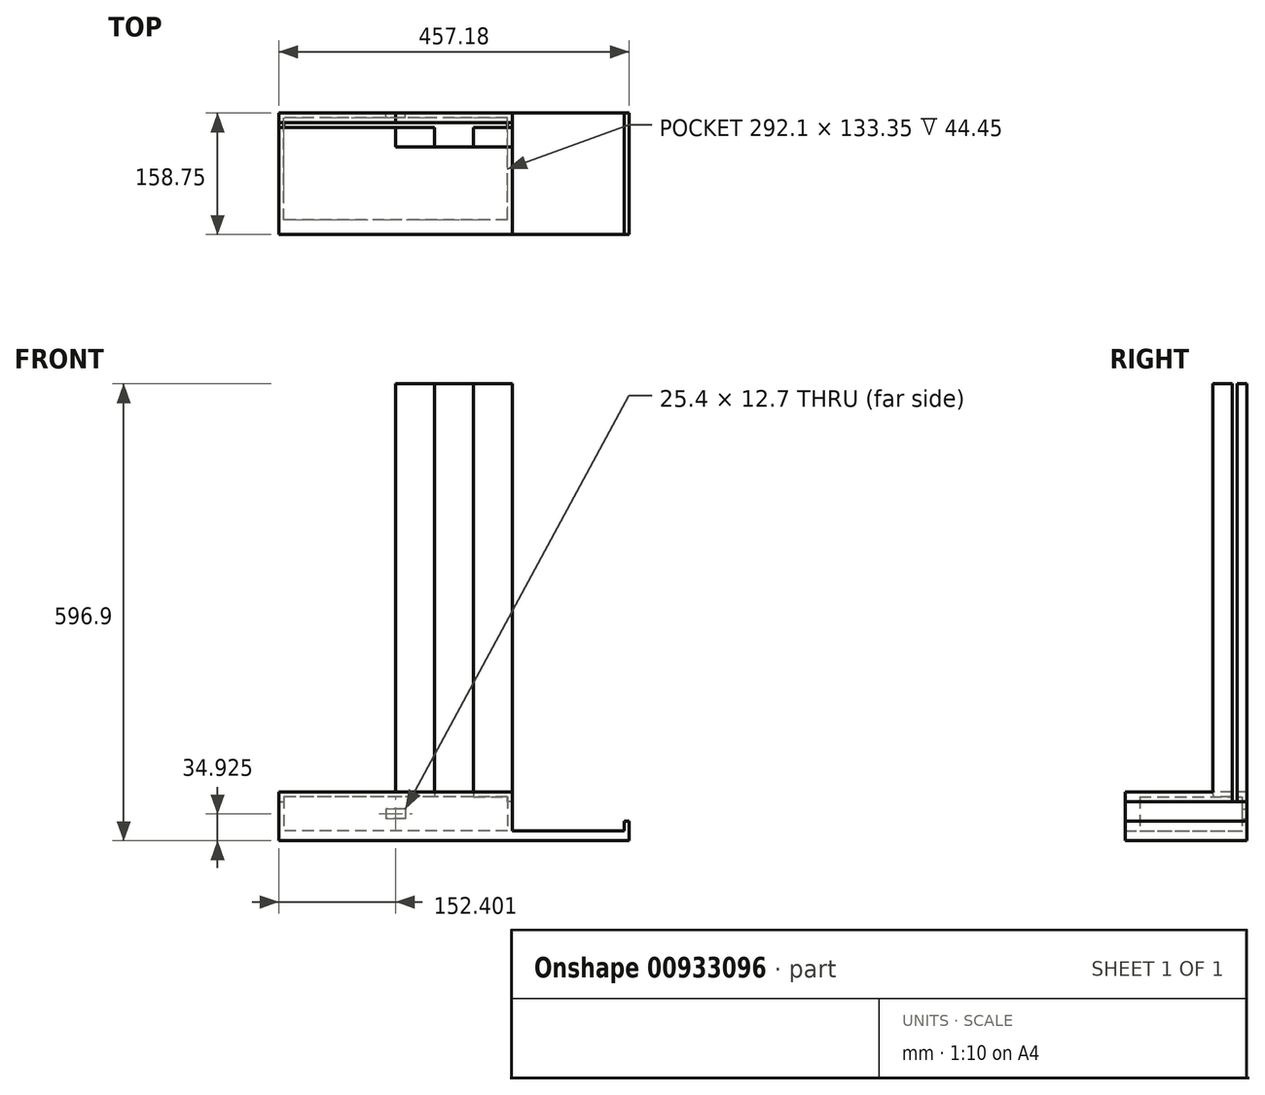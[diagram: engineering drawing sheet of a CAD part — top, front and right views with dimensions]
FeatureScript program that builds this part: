
annotation { "Feature Type Name" : "Feature", "Feature Type Description" : "" }
export const myFeature = defineFeature(function(context is Context, id is Id, definition is map)
    precondition{}
    {
        {
            var Q0;
            Q0=qCreatedBy(makeId("Top.planeOp"),FACE);
            var sketch = newSketch(context, id + "F0", { "sketchPlane" : qUnion([Q0])});
            skLineSegment(sketch, "E0.bottom", {"start": v(-59.49, 68.51) * mm, "end": v(-8.69, 68.51) * mm});
            skLineSegment(sketch, "E0.top", {"start": v(-59.49, 93.91) * mm, "end": v(-8.69, 93.91) * mm});
            skLineSegment(sketch, "E0.left", {"start": v(-59.49, 68.51) * mm, "end": v(-59.49, 93.91) * mm});
            skLineSegment(sketch, "E0.right", {"start": v(-8.69, 68.51) * mm, "end": v(-8.69, 93.91) * mm});
            skLineSegment(sketch, "E1.bottom", {"start": v(92.91, 68.51) * mm, "end": v(42.11, 68.51) * mm});
            skLineSegment(sketch, "E1.top", {"start": v(92.91, 93.91) * mm, "end": v(42.11, 93.91) * mm});
            skLineSegment(sketch, "E1.left", {"start": v(92.91, 68.51) * mm, "end": v(92.91, 93.91) * mm});
            skLineSegment(sketch, "E1.right", {"start": v(42.11, 68.51) * mm, "end": v(42.11, 93.91) * mm});
            skLineSegment(sketch, "E2.bottom", {"start": v(92.91, 93.91) * mm, "end": v(54.81, 93.91) * mm});
            skLineSegment(sketch, "E2.top", {"start": v(92.91, 100.26) * mm, "end": v(54.81, 100.26) * mm});
            skLineSegment(sketch, "E2.left", {"start": v(92.91, 93.91) * mm, "end": v(92.91, 100.26) * mm});
            skLineSegment(sketch, "E2.right", {"start": v(54.81, 93.91) * mm, "end": v(54.81, 100.26) * mm});
            skLineSegment(sketch, "E3.bottom", {"start": v(-59.49, 93.91) * mm, "end": v(-21.39, 93.91) * mm});
            skLineSegment(sketch, "E3.top", {"start": v(-59.49, 100.26) * mm, "end": v(-21.39, 100.26) * mm});
            skLineSegment(sketch, "E3.left", {"start": v(-59.49, 93.91) * mm, "end": v(-59.49, 100.26) * mm});
            skLineSegment(sketch, "E3.right", {"start": v(-21.39, 93.91) * mm, "end": v(-21.39, 100.26) * mm});
            skLineSegment(sketch, "E4.bottom", {"start": v(-59.49, 100.26) * mm, "end": v(92.91, 100.26) * mm});
            skLineSegment(sketch, "E4.top", {"start": v(-59.49, 112.96) * mm, "end": v(92.91, 112.96) * mm});
            skLineSegment(sketch, "E4.left", {"start": v(-59.49, 100.26) * mm, "end": v(-59.49, 112.96) * mm});
            skLineSegment(sketch, "E4.right", {"start": v(92.91, 100.26) * mm, "end": v(92.91, 112.96) * mm});
            skSolve(sketch);
        }
        {
            var Q0;
            Q0=makeQuery(id+"F0.imprint","IMPRINT",FACE,{"disambiguationData":[TD([[makeQuery(id+"F0.imprint","IMPRINT",EDGE,{"derivedFrom":sQuery(id+"F0.wireOp",EDGE,"E4.top")}),-1.0]])]});
            var Q1;
            Q1=makeQuery(id+"F0.imprint","IMPRINT",FACE,{"disambiguationData":[TD([[makeQuery(id+"F0.imprint","IMPRINT",EDGE,{"derivedFrom":sQuery(id+"F0.wireOp",EDGE,"E2.bottom")}),-1.0]])]});
            var Q2;
            Q2=makeQuery(id+"F0.imprint","IMPRINT",FACE,{"disambiguationData":[TD([[makeQuery(id+"F0.imprint","IMPRINT",EDGE,{"derivedFrom":sQuery(id+"F0.wireOp",EDGE,"E1.bottom")}),-1.0]])]});
            var Q3;
            Q3=makeQuery(id+"F0.imprint","IMPRINT",FACE,{"disambiguationData":[TD([[makeQuery(id+"F0.imprint","IMPRINT",EDGE,{"derivedFrom":sQuery(id+"F0.wireOp",EDGE,"E3.bottom")}),1.0]])]});
            var Q4;
            Q4=makeQuery(id+"F0.imprint","IMPRINT",FACE,{"disambiguationData":[TD([[makeQuery(id+"F0.imprint","IMPRINT",EDGE,{"derivedFrom":sQuery(id+"F0.wireOp",EDGE,"E0.bottom")}),1.0]])]});
            extrude(context, id + "F1", {"entities" : qUnion([Q0, Q1, Q2, Q3, Q4]), "depth" : 546.1 * mm, "offsetDistance" : 25.4 * mm});
        }
        {
            var Q0;
            Q0=makeQuery(id+"F1.opExtrude","CAP_FACE",FACE,{"disambiguationData":[OSD([sQuery(id+"F0.wireOp",EDGE,"E0.bottom"),sQuery(id+"F0.wireOp",EDGE,"E0.top"),sQuery(id+"F0.wireOp",EDGE,"E0.left"),sQuery(id+"F0.wireOp",EDGE,"E0.right"),sQuery(id+"F0.wireOp",EDGE,"E1.bottom"),sQuery(id+"F0.wireOp",EDGE,"E1.top"),sQuery(id+"F0.wireOp",EDGE,"E1.left"),sQuery(id+"F0.wireOp",EDGE,"E1.right"),sQuery(id+"F0.wireOp",EDGE,"E2.left"),sQuery(id+"F0.wireOp",EDGE,"E2.right"),sQuery(id+"F0.wireOp",EDGE,"E3.left"),sQuery(id+"F0.wireOp",EDGE,"E3.right"),sQuery(id+"F0.wireOp",EDGE,"E4.bottom"),sQuery(id+"F0.wireOp",EDGE,"E4.top"),sQuery(id+"F0.wireOp",EDGE,"E4.left"),sQuery(id+"F0.wireOp",EDGE,"E4.right")])],"isStart":true});
            var sketch = newSketch(context, id + "F2", { "sketchPlane" : qUnion([Q0])});
            skLineSegment(sketch, "E5.bottom", {"start": v(-59.49, -68.51) * mm, "end": v(92.91, -68.51) * mm});
            skLineSegment(sketch, "E5.top", {"start": v(-59.49, 45.79) * mm, "end": v(92.91, 45.79) * mm});
            skLineSegment(sketch, "E5.left", {"start": v(-59.49, -68.51) * mm, "end": v(-59.49, 45.79) * mm});
            skLineSegment(sketch, "E5.right", {"start": v(92.91, -68.51) * mm, "end": v(92.91, 45.79) * mm});
            skSolve(sketch);
        }
        {
            var Q0;
            Q0=makeQuery(id+"F2.imprint","IMPRINT",FACE,{"disambiguationData":[TD([[makeQuery(id+"F2.imprint","IMPRINT",EDGE,{"derivedFrom":sQuery(id+"F2.wireOp",EDGE,"E5.top")}),-1.0]])]});
            extrude(context, id + "F3", {"entities" : qUnion([Q0]), "operationType" : NewBodyOperationType.ADD, "oppositeDirection" : true, "depth" : 12.7 * mm, "offsetDistance" : 25.4 * mm});
        }
        {
            var Q0;
            Q0=makeQuery(id+"F3.boolean.opBoolean","MERGE",FACE,{"derivedFrom":[makeQuery(id+"F1.opExtrude","CAP_FACE",FACE,{"disambiguationData":[OSD([sQuery(id+"F0.wireOp",EDGE,"E0.bottom"),sQuery(id+"F0.wireOp",EDGE,"E0.top"),sQuery(id+"F0.wireOp",EDGE,"E0.left"),sQuery(id+"F0.wireOp",EDGE,"E0.right"),sQuery(id+"F0.wireOp",EDGE,"E1.bottom"),sQuery(id+"F0.wireOp",EDGE,"E1.top"),sQuery(id+"F0.wireOp",EDGE,"E1.left"),sQuery(id+"F0.wireOp",EDGE,"E1.right"),sQuery(id+"F0.wireOp",EDGE,"E2.left"),sQuery(id+"F0.wireOp",EDGE,"E2.right"),sQuery(id+"F0.wireOp",EDGE,"E3.left"),sQuery(id+"F0.wireOp",EDGE,"E3.right"),sQuery(id+"F0.wireOp",EDGE,"E4.bottom"),sQuery(id+"F0.wireOp",EDGE,"E4.top"),sQuery(id+"F0.wireOp",EDGE,"E4.left"),sQuery(id+"F0.wireOp",EDGE,"E4.right")])],"isStart":true}),makeQuery(id+"F3.opExtrude","CAP_FACE",FACE,{"disambiguationData":[OSD([sQuery(id+"F2.wireOp",EDGE,"E5.bottom"),sQuery(id+"F2.wireOp",EDGE,"E5.top"),sQuery(id+"F2.wireOp",EDGE,"E5.left"),sQuery(id+"F2.wireOp",EDGE,"E5.right")])],"isStart":true})]});
            var sketch = newSketch(context, id + "F4", { "sketchPlane" : qUnion([Q0])});
            skLineSegment(sketch, "E6.bottom", {"start": v(-59.49, 45.79) * mm, "end": v(92.89, 45.79) * mm});
            skLineSegment(sketch, "E6.top", {"start": v(-59.49, -112.96) * mm, "end": v(92.89, -112.96) * mm});
            skLineSegment(sketch, "E6.left", {"start": v(-59.49, 45.79) * mm, "end": v(-59.49, -112.96) * mm});
            skLineSegment(sketch, "E6.right", {"start": v(92.89, 45.79) * mm, "end": v(92.89, -112.96) * mm});
            skSolve(sketch);
        }
        {
            var Q0;
            Q0 = qSketchRegion(id + "F4", true);
            extrude(context, id + "F5", {"entities" : qUnion([Q0]), "operationType" : NewBodyOperationType.ADD, "depth" : 50.8 * mm, "offsetDistance" : 25.4 * mm});
        }
        {
            var Q0;
            Q0=makeQuery(id+"F5.opExtrude","SWEPT_FACE",FACE,{"disambiguationData":[OSD([sQuery(id+"F4.wireOp",EDGE,"E6.right")])]});
            var sketch = newSketch(context, id + "F6", { "sketchPlane" : qUnion([Q0])});
            skLineSegment(sketch, "E7.bottom", {"start": v(-45.79, -38.1) * mm, "end": v(112.96, -38.1) * mm});
            skLineSegment(sketch, "E7.top", {"start": v(-45.79, -50.8) * mm, "end": v(112.96, -50.8) * mm});
            skLineSegment(sketch, "E7.left", {"start": v(-45.79, -38.1) * mm, "end": v(-45.79, -50.8) * mm});
            skLineSegment(sketch, "E7.right", {"start": v(112.96, -38.1) * mm, "end": v(112.96, -50.8) * mm});
            skSolve(sketch);
        }
        {
            var Q0;
            Q0=makeQuery(id+"F6.imprint","IMPRINT",FACE,{"disambiguationData":[TD([[makeQuery(id+"F6.imprint","IMPRINT",EDGE,{"derivedFrom":sQuery(id+"F6.wireOp",EDGE,"E7.bottom")}),-1.0]])]});
            extrude(context, id + "F7", {"entities" : qUnion([Q0]), "operationType" : NewBodyOperationType.ADD, "depth" : 152.4 * mm, "offsetDistance" : 25.4 * mm});
        }
        {
            var Q0;
            Q0=makeQuery(id+"F7.opExtrude","SWEPT_FACE",FACE,{"disambiguationData":[OSD([sQuery(id+"F6.wireOp",EDGE,"E7.bottom")])]});
            var sketch = newSketch(context, id + "F8", { "sketchPlane" : qUnion([Q0])});
            skLineSegment(sketch, "E8.bottom", {"start": v(245.29, -45.79) * mm, "end": v(238.94, -45.79) * mm});
            skLineSegment(sketch, "E8.top", {"start": v(245.29, 112.96) * mm, "end": v(238.94, 112.96) * mm});
            skLineSegment(sketch, "E8.left", {"start": v(245.29, -45.79) * mm, "end": v(245.29, 112.96) * mm});
            skLineSegment(sketch, "E8.right", {"start": v(238.94, -45.79) * mm, "end": v(238.94, 112.96) * mm});
            skSolve(sketch);
        }
        {
            var Q0;
            Q0=makeQuery(id+"F8.imprint","IMPRINT",FACE,{"disambiguationData":[TD([[makeQuery(id+"F8.imprint","IMPRINT",EDGE,{"derivedFrom":sQuery(id+"F8.wireOp",EDGE,"E8.bottom")}),-1.0]])]});
            extrude(context, id + "F9", {"entities" : qUnion([Q0]), "operationType" : NewBodyOperationType.ADD, "depth" : 12.7 * mm, "offsetDistance" : 25.4 * mm});
        }
        {
            var Q0;
            Q0=makeQuery(id+"F5.boolean.opBoolean","MERGE",FACE,{"derivedFrom":[makeQuery(id+"F3.boolean.opBoolean","MERGE",FACE,{"derivedFrom":[makeQuery(id+"F1.opExtrude","SWEPT_FACE",FACE,{"disambiguationData":[OSD([sQuery(id+"F0.wireOp",EDGE,"E0.left"),sQuery(id+"F0.wireOp",EDGE,"E3.left"),sQuery(id+"F0.wireOp",EDGE,"E4.left")])]}),makeQuery(id+"F3.opExtrude","SWEPT_FACE",FACE,{"disambiguationData":[OSD([sQuery(id+"F2.wireOp",EDGE,"E5.left")])]})]}),makeQuery(id+"F5.opExtrude","SWEPT_FACE",FACE,{"disambiguationData":[OSD([sQuery(id+"F4.wireOp",EDGE,"E6.left")])]})]});
            var sketch = newSketch(context, id + "F10", { "sketchPlane" : qUnion([Q0])});
            skLineSegment(sketch, "E9.bottom", {"start": v(-112.96, -50.8) * mm, "end": v(45.79, -50.8) * mm});
            skLineSegment(sketch, "E9.top", {"start": v(-112.96, 12.7) * mm, "end": v(45.79, 12.7) * mm});
            skLineSegment(sketch, "E9.left", {"start": v(-112.96, -50.8) * mm, "end": v(-112.96, 12.7) * mm});
            skLineSegment(sketch, "E9.right", {"start": v(45.79, -50.8) * mm, "end": v(45.79, 12.7) * mm});
            skSolve(sketch);
        }
        {
            var Q0;
            Q0=makeQuery(id+"F10.imprint","IMPRINT",FACE,{"disambiguationData":[TD([[makeQuery(id+"F10.imprint","IMPRINT",EDGE,{"derivedFrom":sQuery(id+"F10.wireOp",EDGE,"E9.bottom")}),-1.0]])]});
            extrude(context, id + "F11", {"entities" : qUnion([Q0]), "operationType" : NewBodyOperationType.ADD, "depth" : 152.4 * mm, "offsetDistance" : 25.4 * mm});
        }
        {
            var Q0;
            Q0=makeQuery(id+"F11.boolean.opBoolean","MERGE",FACE,{"derivedFrom":[makeQuery(id+"F9.boolean.opBoolean","MERGE",FACE,{"derivedFrom":[makeQuery(id+"F7.boolean.opBoolean","MERGE",FACE,{"derivedFrom":[makeQuery(id+"F5.boolean.opBoolean","MERGE",FACE,{"derivedFrom":[makeQuery(id+"F1.opExtrude","SWEPT_FACE",FACE,{"disambiguationData":[OSD([sQuery(id+"F0.wireOp",EDGE,"E4.top")])]}),makeQuery(id+"F5.opExtrude","SWEPT_FACE",FACE,{"disambiguationData":[OSD([sQuery(id+"F4.wireOp",EDGE,"E6.top")])]})]}),makeQuery(id+"F7.opExtrude","SWEPT_FACE",FACE,{"disambiguationData":[OSD([sQuery(id+"F6.wireOp",EDGE,"E7.right")])]})]}),makeQuery(id+"F9.opExtrude","SWEPT_FACE",FACE,{"disambiguationData":[OSD([sQuery(id+"F8.wireOp",EDGE,"E8.top")])]})]}),makeQuery(id+"F11.opExtrude","SWEPT_FACE",FACE,{"disambiguationData":[OSD([sQuery(id+"F10.wireOp",EDGE,"E9.left")])]})]});
            var sketch = newSketch(context, id + "F12", { "sketchPlane" : qUnion([Q0])});
            skLineSegment(sketch, "E10.bottom", {"start": v(-86.56, 6.35) * mm, "end": v(205.54, 6.35) * mm});
            skLineSegment(sketch, "E10.top", {"start": v(-86.56, -38.1) * mm, "end": v(205.54, -38.1) * mm});
            skLineSegment(sketch, "E10.left", {"start": v(-86.56, 6.35) * mm, "end": v(-86.56, -38.1) * mm});
            skLineSegment(sketch, "E10.right", {"start": v(205.54, 6.35) * mm, "end": v(205.54, -38.1) * mm});
            skSolve(sketch);
        }
        {
            var Q0;
            Q0=makeQuery(id+"F12.imprint","IMPRINT",FACE,{"disambiguationData":[TD([[makeQuery(id+"F12.imprint","IMPRINT",EDGE,{"derivedFrom":sQuery(id+"F12.wireOp",EDGE,"E10.bottom")}),-1.0]])]});
            extrude(context, id + "F13", {"entities" : qUnion([Q0]), "operationType" : NewBodyOperationType.REMOVE, "oppositeDirection" : true, "depth" : 139.7 * mm, "offsetDistance" : 25.4 * mm});
        }
        {
            var Q0;
            Q0=makeQuery(id+"F11.boolean.opBoolean","MERGE",FACE,{"derivedFrom":[makeQuery(id+"F9.boolean.opBoolean","MERGE",FACE,{"derivedFrom":[makeQuery(id+"F7.boolean.opBoolean","MERGE",FACE,{"derivedFrom":[makeQuery(id+"F5.boolean.opBoolean","MERGE",FACE,{"derivedFrom":[makeQuery(id+"F1.opExtrude","SWEPT_FACE",FACE,{"disambiguationData":[OSD([sQuery(id+"F0.wireOp",EDGE,"E4.top")])]}),makeQuery(id+"F5.opExtrude","SWEPT_FACE",FACE,{"disambiguationData":[OSD([sQuery(id+"F4.wireOp",EDGE,"E6.top")])]})]}),makeQuery(id+"F7.opExtrude","SWEPT_FACE",FACE,{"disambiguationData":[OSD([sQuery(id+"F6.wireOp",EDGE,"E7.right")])]})]}),makeQuery(id+"F9.opExtrude","SWEPT_FACE",FACE,{"disambiguationData":[OSD([sQuery(id+"F8.wireOp",EDGE,"E8.top")])]})]}),makeQuery(id+"F11.opExtrude","SWEPT_FACE",FACE,{"disambiguationData":[OSD([sQuery(id+"F10.wireOp",EDGE,"E9.left")])]})]});
            var sketch = newSketch(context, id + "F14", { "sketchPlane" : qUnion([Q0])});
            skLineSegment(sketch, "E11.bottom", {"start": v(-86.56, 6.35) * mm, "end": v(205.54, 6.35) * mm});
            skLineSegment(sketch, "E11.top", {"start": v(-86.56, -38.1) * mm, "end": v(205.54, -38.1) * mm});
            skLineSegment(sketch, "E11.left", {"start": v(-86.56, 6.35) * mm, "end": v(-86.56, -38.1) * mm});
            skLineSegment(sketch, "E11.right", {"start": v(205.54, 6.35) * mm, "end": v(205.54, -38.1) * mm});
            skLineSegment(sketch, "E12.bottom", {"start": v(46.79, -9.52) * mm, "end": v(72.19, -9.52) * mm});
            skLineSegment(sketch, "E12.top", {"start": v(46.79, -22.22) * mm, "end": v(72.19, -22.22) * mm});
            skLineSegment(sketch, "E12.left", {"start": v(46.79, -9.52) * mm, "end": v(46.79, -22.22) * mm});
            skLineSegment(sketch, "E12.right", {"start": v(72.19, -9.52) * mm, "end": v(72.19, -22.22) * mm});
            skSolve(sketch);
        }
        {
            var Q0;
            Q0=makeQuery(id+"F14.imprint","IMPRINT",FACE,{"disambiguationData":[TD([[makeQuery(id+"F14.imprint","IMPRINT",EDGE,{"derivedFrom":sQuery(id+"F14.wireOp",EDGE,"E11.bottom")}),-1.0]])]});
            extrude(context, id + "F15", {"entities" : qUnion([Q0]), "operationType" : NewBodyOperationType.ADD, "oppositeDirection" : true, "depth" : 6.35 * mm, "offsetDistance" : 25.4 * mm});
        }
    });
